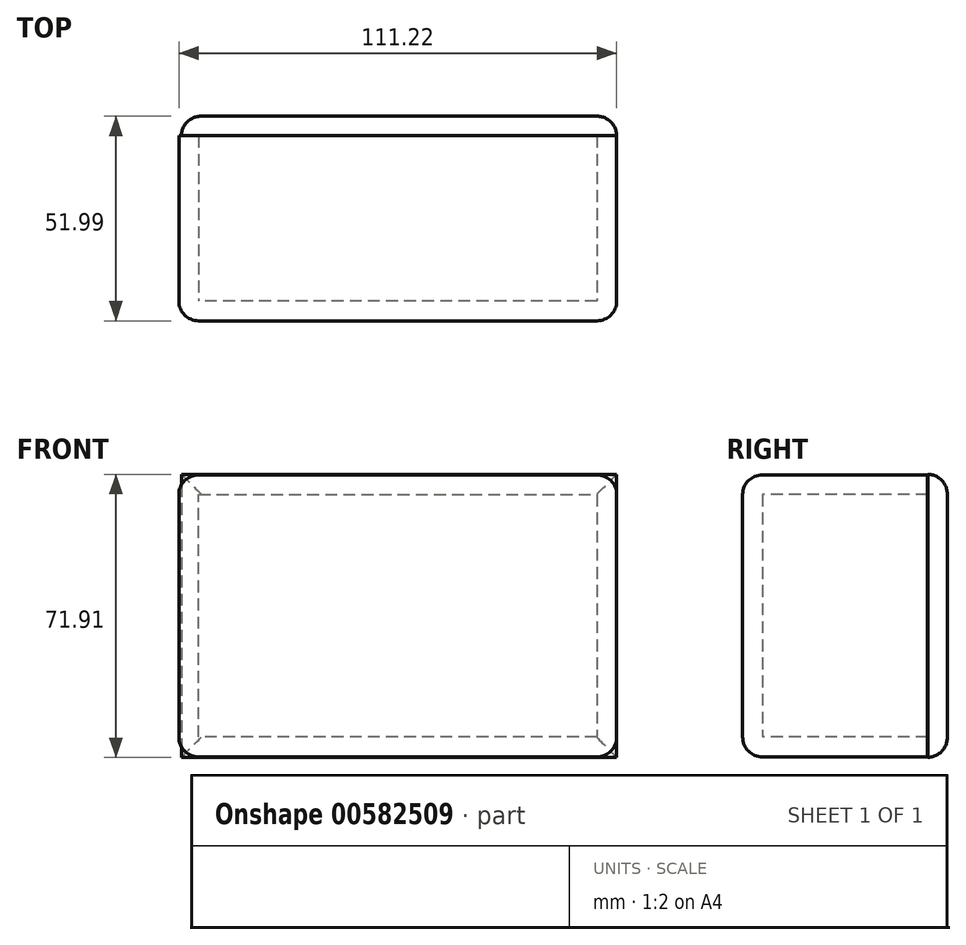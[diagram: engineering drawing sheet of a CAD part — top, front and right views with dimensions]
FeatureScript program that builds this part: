
annotation { "Feature Type Name" : "Feature", "Feature Type Description" : "" }
export const myFeature = defineFeature(function(context is Context, id is Id, definition is map)
    precondition{}
    {
        {
            var Q0;
            Q0=qCreatedBy(makeId("Front.planeOp"),FACE);
            var sketch = newSketch(context, id + "F0", { "sketchPlane" : qUnion([Q0])});
            skLineSegment(sketch, "E0.bottom", {"start": v(0, 0) * mm, "end": v(-101.22, 0) * mm});
            skLineSegment(sketch, "E0.top", {"start": v(0, 61.63) * mm, "end": v(-101.22, 61.63) * mm});
            skLineSegment(sketch, "E0.left", {"start": v(0, 0) * mm, "end": v(0, 61.63) * mm});
            skLineSegment(sketch, "E0.right", {"start": v(-101.22, 0) * mm, "end": v(-101.22, 61.63) * mm});
            skArc(sketch, "E1", {"start": v(-101.22, 66.63) * mm, "mid": v(-104.76, 65.17) * mm, "end": v(-106.22, 61.63) * mm});
            skArc(sketch, "E2", {"start": v(-106.22, 0) * mm, "mid": v(-104.76, -3.54) * mm, "end": v(-101.22, -5) * mm});
            skArc(sketch, "E3", {"start": v(0, -5) * mm, "mid": v(3.54, -3.54) * mm, "end": v(5, 0) * mm});
            skArc(sketch, "E4", {"start": v(5, 61.63) * mm, "mid": v(3.54, 65.17) * mm, "end": v(0, 66.63) * mm});
            skLineSegment(sketch, "E5", {"start": v(-101.22, -5) * mm, "end": v(0, -5) * mm});
            skLineSegment(sketch, "E6", {"start": v(5, 0) * mm, "end": v(5, 61.63) * mm});
            skLineSegment(sketch, "E7", {"start": v(0, 66.63) * mm, "end": v(-101.22, 66.63) * mm});
            skPoint(sketch, "E8.end.orphan", {"position": v(-106.22, 0) * mm});
            skLineSegment(sketch, "E9", {"start": v(-106.22, 0) * mm, "end": v(-106.22, 61.63) * mm});
            skSolve(sketch);
        }
        {
            var Q0;
            Q0=makeQuery(id+"F0.imprint","IMPRINT",FACE,{"disambiguationData":[TD([[makeQuery(id+"F0.imprint","IMPRINT",EDGE,{"derivedFrom":sQuery(id+"F0.wireOp",EDGE,"E0.bottom")}),-1.0]])]});
            var Q1;
            Q1=makeQuery(id+"F0.imprint","IMPRINT",FACE,{"disambiguationData":[TD([[makeQuery(id+"F0.imprint","IMPRINT",EDGE,{"derivedFrom":sQuery(id+"F0.wireOp",EDGE,"E0.bottom")}),1.0]])]});
            extrude(context, id + "F1", {"entities" : qUnion([Q0, Q1]), "depth" : 5 * mm, "offsetDistance" : 25 * mm});
        }
        {
            var Q0;
            Q0=makeQuery(id+"F1.opExtrude","CAP_EDGE",EDGE,{"disambiguationData":[OSD([sQuery(id+"F0.wireOp",EDGE,"E5")])],"isStart":false});
            fillet(context, id + "F2", {"entities" : qUnion([Q0]), "radius" : 5 * mm, "tangentPropagation" : true, "allowEdgeOverflow" : false});
        }
        {
            var Q0;
            Q0=makeQuery(id+"F1.opExtrude","CAP_FACE",FACE,{"disambiguationData":[OSD([sQuery(id+"F0.wireOp",EDGE,"E1"),sQuery(id+"F0.wireOp",EDGE,"E2"),sQuery(id+"F0.wireOp",EDGE,"E3"),sQuery(id+"F0.wireOp",EDGE,"E4"),sQuery(id+"F0.wireOp",EDGE,"E5"),sQuery(id+"F0.wireOp",EDGE,"E6"),sQuery(id+"F0.wireOp",EDGE,"E7"),sQuery(id+"F0.wireOp",EDGE,"E9")])],"isStart":true});
            var sketch = newSketch(context, id + "F3", { "sketchPlane" : qUnion([Q0])});
            skLineSegment(sketch, "E10", {"start": v(0, 0) * mm, "end": v(101.22, 0) * mm});
            skLineSegment(sketch, "E11", {"start": v(101.22, 0) * mm, "end": v(101.22, 61.63) * mm});
            skLineSegment(sketch, "E12", {"start": v(101.22, 61.63) * mm, "end": v(0, 61.63) * mm});
            skLineSegment(sketch, "E13", {"start": v(0, 61.63) * mm, "end": v(0, 0) * mm});
            skSolve(sketch);
        }
        {
            var Q0;
            Q0=makeQuery(id+"F3.imprint","IMPRINT",FACE,{"disambiguationData":[TD([[makeQuery(id+"F3.imprint","IMPRINT",EDGE,{"derivedFrom":sQuery(id+"F3.wireOp",EDGE,"E10")}),1.0]])]});
            cPlane(context, id + "F4", {"entities" : qUnion([Q0]), "cplaneType" : CPlaneType.OFFSET, "offset" : 37 * mm, "width" : 150 * mm, "height" : 150 * mm});
        }
        {
            var Q0;
            Q0=makeQuery(id+"F3.imprint","IMPRINT",FACE,{"disambiguationData":[TD([[makeQuery(id+"F3.imprint","IMPRINT",EDGE,{"derivedFrom":sQuery(id+"F3.wireOp",EDGE,"E10")}),-1.0]])]});
            extrude(context, id + "F5", {"entities" : qUnion([Q0]), "operationType" : NewBodyOperationType.ADD, "depth" : 42 * mm, "offsetDistance" : 25 * mm});
        }
        {
            var Q0;
            {var subQ0=sQuery(id+"F0.wireOp",EDGE,"E9");var subQ1=sQuery(id+"F0.wireOp",EDGE,"E7");var subQ2=sQuery(id+"F0.wireOp",EDGE,"E6");var subQ3=sQuery(id+"F0.wireOp",EDGE,"E5");var subQ4=sQuery(id+"F0.wireOp",EDGE,"E4");var subQ5=sQuery(id+"F0.wireOp",EDGE,"E3");var subQ6=sQuery(id+"F0.wireOp",EDGE,"E2");var subQ7=sQuery(id+"F0.wireOp",EDGE,"E1");Q0=makeQuery(id+"F5.opExtrude","SWEPT_FACE",FACE,{"disambiguationData":[OSD([subQ7,subQ6,subQ5,subQ4,subQ3,subQ2,subQ1,subQ0]),TDD([makeQuery(id+"F3.imprint","IMPRINT",EDGE,{"derivedFrom":makeQuery(id+"F2.opFillet","BLEND_EDGE",EDGE,{"blendedFrom":[makeQuery(id+"F1.opExtrude","CAP_EDGE",EDGE,{"disambiguationData":[OSD([subQ2])],"isStart":false}),makeQuery(id+"F1.opExtrude","CAP_FACE",FACE,{"disambiguationData":[OSD([subQ7,subQ6,subQ5,subQ4,subQ3,subQ2,subQ1,subQ0])],"isStart":true})],"blendedInto":[makeQuery(id+"F1.opExtrude","CAP_FACE",FACE,{"disambiguationData":[OSD([subQ7,subQ6,subQ5,subQ4,subQ3,subQ2,subQ1,subQ0])],"isStart":true})]})})])]});}
            var sketch = newSketch(context, id + "F6", { "sketchPlane" : qUnion([Q0])});
            skLineSegment(sketch, "E14.bottom", {"start": v(42.11, 66.78) * mm, "end": v(46.99, 66.78) * mm});
            skLineSegment(sketch, "E14.top", {"start": v(42.11, -5.13) * mm, "end": v(46.99, -5.13) * mm});
            skLineSegment(sketch, "E14.left", {"start": v(42.11, 66.78) * mm, "end": v(42.11, -5.13) * mm});
            skLineSegment(sketch, "E14.right", {"start": v(46.99, 66.78) * mm, "end": v(46.99, -5.13) * mm});
            skSolve(sketch);
        }
        {
            var Q0;
            Q0=makeQuery(id+"F6.imprint","IMPRINT",FACE,{"disambiguationData":[TD([[makeQuery(id+"F6.imprint","IMPRINT",EDGE,{"derivedFrom":sQuery(id+"F6.wireOp",EDGE,"E14.bottom")}),-1.0]])]});
            extrude(context, id + "F7", {"entities" : qUnion([Q0]), "oppositeDirection" : true, "depth" : 110.6 * mm, "offsetDistance" : 25 * mm});
        }
        {
            var Q0;
            Q0=makeQuery(id+"F7.opExtrude","CAP_EDGE",EDGE,{"disambiguationData":[OSD([sQuery(id+"F6.wireOp",EDGE,"E14.right")])],"isStart":true});
            var Q1;
            Q1=makeQuery(id+"F7.opExtrude","SWEPT_EDGE",EDGE,{"disambiguationData":[OSD([sQuery(id+"F6.wireOp",EDGE,"E14.bottom"),sQuery(id+"F6.wireOp",EDGE,"E14.right")])]});
            var Q2;
            Q2=makeQuery(id+"F7.opExtrude","CAP_EDGE",EDGE,{"disambiguationData":[OSD([sQuery(id+"F6.wireOp",EDGE,"E14.right")])],"isStart":false});
            var Q3;
            Q3=makeQuery(id+"F7.opExtrude","SWEPT_EDGE",EDGE,{"disambiguationData":[OSD([sQuery(id+"F6.wireOp",EDGE,"E14.top"),sQuery(id+"F6.wireOp",EDGE,"E14.right")])]});
            fillet(context, id + "F8", {"entities" : qUnion([Q0, Q1, Q2, Q3]), "radius" : 5 * mm, "tangentPropagation" : true, "allowEdgeOverflow" : false});
        }
    });
